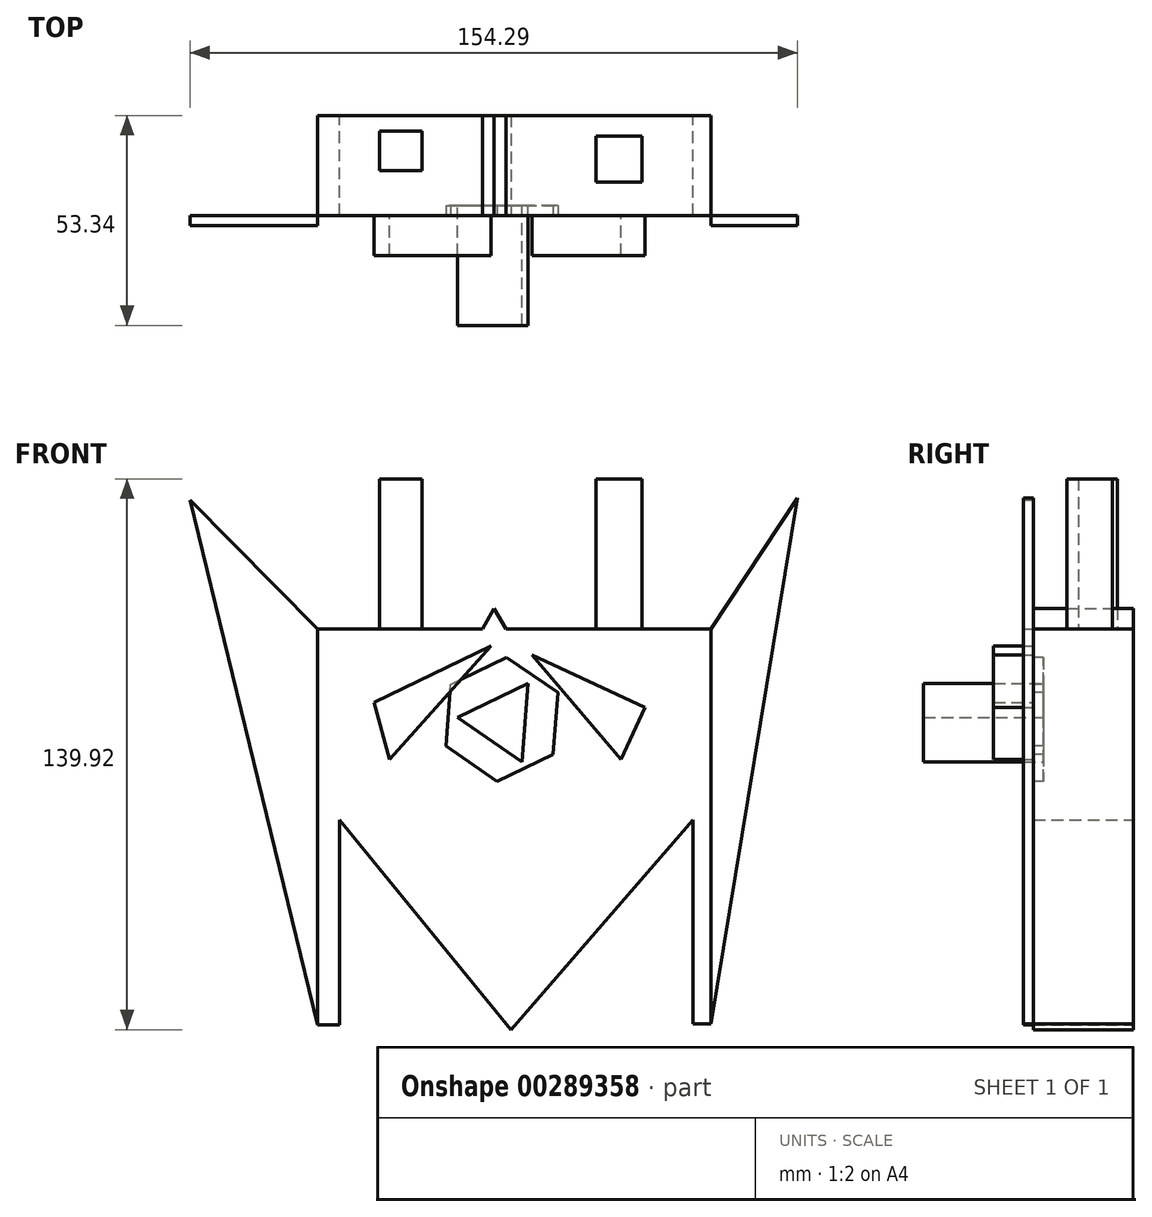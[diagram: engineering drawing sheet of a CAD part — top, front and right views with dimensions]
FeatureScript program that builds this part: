
annotation { "Feature Type Name" : "Feature", "Feature Type Description" : "" }
export const myFeature = defineFeature(function(context is Context, id is Id, definition is map)
    precondition{}
    {
        {
            var Q0;
            Q0=qCreatedBy(makeId("Front.planeOp"),FACE);
            var sketch = newSketch(context, id + "F0", { "sketchPlane" : qUnion([Q0])});
            skLineSegment(sketch, "E0.bottom", {"start": v(-40.98, 12.79) * mm, "end": v(-35.41, 12.79) * mm});
            skLineSegment(sketch, "E0.top", {"start": v(-40.98, -39.35) * mm, "end": v(-35.41, -39.35) * mm});
            skLineSegment(sketch, "E0.left", {"start": v(-40.98, 12.79) * mm, "end": v(-40.98, -39.35) * mm});
            skLineSegment(sketch, "E0.right", {"start": v(-35.41, 12.79) * mm, "end": v(-35.41, -39.35) * mm});
            skLineSegment(sketch, "E1.bottom", {"start": v(-40.98, 12.79) * mm, "end": v(59.02, 12.79) * mm});
            skLineSegment(sketch, "E1.top", {"start": v(-40.98, 61.31) * mm, "end": v(59.02, 61.31) * mm});
            skLineSegment(sketch, "E1.left", {"start": v(-40.98, 12.79) * mm, "end": v(-40.98, 61.31) * mm});
            skLineSegment(sketch, "E1.right", {"start": v(59.02, 12.79) * mm, "end": v(59.02, 61.31) * mm});
            skLineSegment(sketch, "E2.bottom", {"start": v(59.02, 12.79) * mm, "end": v(54.43, 12.79) * mm});
            skLineSegment(sketch, "E2.top", {"start": v(59.02, -39.02) * mm, "end": v(54.43, -39.02) * mm});
            skLineSegment(sketch, "E2.left", {"start": v(59.02, 12.79) * mm, "end": v(59.02, -39.02) * mm});
            skLineSegment(sketch, "E2.right", {"start": v(54.43, 12.79) * mm, "end": v(54.43, -39.02) * mm});
            skArc(sketch, "E3", {"start": v(9.18, -21.31) * mm, "mid": v(3.35, -2.92) * mm, "end": v(-7.87, 12.79) * mm});
            skArc(sketch, "E4", {"start": v(9.18, -21.31) * mm, "mid": v(19.12, -5.56) * mm, "end": v(22.3, 12.79) * mm});
            skArc(sketch, "E5", {"start": v(-2.03, 5.92) * mm, "mid": v(-8, -5.66) * mm, "end": v(-7.87, -18.69) * mm});
            skArc(sketch, "E6", {"start": v(-7.87, 12.79) * mm, "mid": v(-18.77, -1.85) * mm, "end": v(-8.2, -16.72) * mm});
            skCircle(sketch, "E7.cCircle", {"center": v(3.93, 42.3) * mm, "radius": 12.13 * mm, "construction": true});
            skLineSegment(sketch, "E7.0", {"start": v(24.95, 30.16) * mm, "end": v(-17.08, 30.16) * mm});
            skLineSegment(sketch, "E7.1", {"start": v(-17.08, 30.16) * mm, "end": v(3.93, 66.56) * mm});
            skLineSegment(sketch, "E7.2", {"start": v(3.93, 66.56) * mm, "end": v(24.95, 30.16) * mm});
            skPoint(sketch, "E7.0.midPoint", {"position": v(3.93, 30.16) * mm});
            skSolve(sketch);
        }
        {
            var Q0;
            Q0 = qSketchRegion(id + "F0", true);
            extrude(context, id + "F1", {"entities" : qUnion([Q0]), "depth" : 25.4 * mm});
        }
        {
            var Q0;
            Q0=makeQuery(id+"F1.opExtrude","CAP_FACE",FACE,{"disambiguationData":[OSD([sQuery(id+"F0.wireOp",EDGE,"E0.top"),sQuery(id+"F0.wireOp",EDGE,"E0.left"),sQuery(id+"F0.wireOp",EDGE,"E0.right"),sQuery(id+"F0.wireOp",EDGE,"E1.bottom"),sQuery(id+"F0.wireOp",EDGE,"E1.top"),sQuery(id+"F0.wireOp",EDGE,"E1.left"),sQuery(id+"F0.wireOp",EDGE,"E1.right"),sQuery(id+"F0.wireOp",EDGE,"E2.top"),sQuery(id+"F0.wireOp",EDGE,"E2.left"),sQuery(id+"F0.wireOp",EDGE,"E2.right"),sQuery(id+"F0.wireOp",EDGE,"E3"),sQuery(id+"F0.wireOp",EDGE,"E4"),sQuery(id+"F0.wireOp",EDGE,"E5"),sQuery(id+"F0.wireOp",EDGE,"E6"),sQuery(id+"F0.wireOp",EDGE,"E7.1"),sQuery(id+"F0.wireOp",EDGE,"E7.2")])],"isStart":false});
            var sketch = newSketch(context, id + "F2", { "sketchPlane" : qUnion([Q0])});
            skCircle(sketch, "E8.cCircle", {"center": v(5.89, 38.32) * mm, "radius": 13.66 * mm, "construction": true});
            skLineSegment(sketch, "E8.0", {"start": v(-7.12, 47.24) * mm, "end": v(7.12, 54.04) * mm});
            skLineSegment(sketch, "E8.1", {"start": v(7.12, 54.04) * mm, "end": v(20.12, 45.12) * mm});
            skLineSegment(sketch, "E8.2", {"start": v(20.12, 45.12) * mm, "end": v(18.9, 29.4) * mm});
            skLineSegment(sketch, "E8.3", {"start": v(18.9, 29.4) * mm, "end": v(4.66, 22.6) * mm});
            skLineSegment(sketch, "E8.4", {"start": v(4.66, 22.6) * mm, "end": v(-8.34, 31.51) * mm});
            skLineSegment(sketch, "E8.5", {"start": v(-8.34, 31.51) * mm, "end": v(-7.12, 47.24) * mm});
            skPoint(sketch, "E8.0.midPoint", {"position": v(0, 50.64) * mm});
            skSolve(sketch);
        }
        {
            var Q0;
            Q0 = qSketchRegion(id + "F2", true);
            extrude(context, id + "F3", {"entities" : qUnion([Q0]), "operationType" : NewBodyOperationType.REMOVE, "oppositeDirection" : true, "depth" : 2.54 * mm});
        }
        {
            var Q0;
            Q0=makeQuery(id+"F1.opExtrude","CAP_FACE",FACE,{"disambiguationData":[OSD([sQuery(id+"F0.wireOp",EDGE,"E0.top"),sQuery(id+"F0.wireOp",EDGE,"E0.left"),sQuery(id+"F0.wireOp",EDGE,"E0.right"),sQuery(id+"F0.wireOp",EDGE,"E1.bottom"),sQuery(id+"F0.wireOp",EDGE,"E1.top"),sQuery(id+"F0.wireOp",EDGE,"E1.left"),sQuery(id+"F0.wireOp",EDGE,"E1.right"),sQuery(id+"F0.wireOp",EDGE,"E2.top"),sQuery(id+"F0.wireOp",EDGE,"E2.left"),sQuery(id+"F0.wireOp",EDGE,"E2.right"),sQuery(id+"F0.wireOp",EDGE,"E3"),sQuery(id+"F0.wireOp",EDGE,"E4"),sQuery(id+"F0.wireOp",EDGE,"E5"),sQuery(id+"F0.wireOp",EDGE,"E6"),sQuery(id+"F0.wireOp",EDGE,"E7.1"),sQuery(id+"F0.wireOp",EDGE,"E7.2")])],"isStart":false});
            var sketch = newSketch(context, id + "F4", { "sketchPlane" : qUnion([Q0])});
            skLineSegment(sketch, "E9", {"start": v(-40.98, -39.35) * mm, "end": v(-73.33, 94.12) * mm});
            skLineSegment(sketch, "E10", {"start": v(-73.33, 94.12) * mm, "end": v(-40.98, 61.31) * mm});
            skLineSegment(sketch, "E11", {"start": v(59.02, 61.31) * mm, "end": v(80.96, 94.54) * mm});
            skLineSegment(sketch, "E12", {"start": v(80.96, 94.54) * mm, "end": v(59.02, -39.02) * mm});
            skSolve(sketch);
        }
        {
            var Q0;
            Q0=makeQuery(id+"F4.imprint","IMPRINT",FACE,{"disambiguationData":[TD([[makeQuery(id+"F4.imprint","IMPRINT",EDGE,{"derivedFrom":sQuery(id+"F4.wireOp",EDGE,"E9")}),-1.0]])]});
            var Q1;
            Q1=makeQuery(id+"F4.imprint","IMPRINT",FACE,{"disambiguationData":[TD([[makeQuery(id+"F4.imprint","IMPRINT",EDGE,{"derivedFrom":sQuery(id+"F4.wireOp",EDGE,"E11")}),-1.0]])]});
            extrude(context, id + "F5", {"entities" : qUnion([Q0, Q1]), "depth" : 2.54 * mm});
        }
        {
            var Q0;
            Q0=makeQuery(id+"F3.boolean.opBoolean","COPY",FACE,{"derivedFrom":makeQuery(id+"F3.opExtrude","CAP_FACE",FACE,{"disambiguationData":[OSD([sQuery(id+"F2.wireOp",EDGE,"E8.0"),sQuery(id+"F2.wireOp",EDGE,"E8.1"),sQuery(id+"F2.wireOp",EDGE,"E8.2"),sQuery(id+"F2.wireOp",EDGE,"E8.3"),sQuery(id+"F2.wireOp",EDGE,"E8.4"),sQuery(id+"F2.wireOp",EDGE,"E8.5")])],"isStart":false})});
            var sketch = newSketch(context, id + "F6", { "sketchPlane" : qUnion([Q0])});
            skCircle(sketch, "E13.cCircle", {"center": v(6.05, 37.94) * mm, "radius": 5.75 * mm, "construction": true});
            skPoint(sketch, "E13.cCircle.perimeterSnap0", {"position": v(11.78, 26) * mm});
            skLineSegment(sketch, "E13.0", {"start": v(12.55, 47.42) * mm, "end": v(11, 27.57) * mm});
            skLineSegment(sketch, "E13.1", {"start": v(11, 27.57) * mm, "end": v(-5.4, 38.84) * mm});
            skLineSegment(sketch, "E13.2", {"start": v(-5.4, 38.84) * mm, "end": v(12.55, 47.42) * mm});
            skPoint(sketch, "E13.0.midPoint", {"position": v(11.78, 37.5) * mm});
            skPoint(sketch, "E13.0.midPoint.positionSnap0", {"position": v(11.78, 26) * mm});
            skSolve(sketch);
        }
        {
            var Q0;
            Q0 = qSketchRegion(id + "F6", true);
            extrude(context, id + "F7", {"entities" : qUnion([Q0]), "operationType" : NewBodyOperationType.ADD, "depth" : 30.48 * mm});
        }
        {
            var Q0;
            {var subQ0=sQuery(id+"F0.wireOp",EDGE,"E1.top");Q0=makeQuery(id+"F1.opExtrude","SWEPT_FACE",FACE,{"disambiguationData":[OSD([subQ0]),TDD([makeQuery(id+"F0.imprint","IMPRINT",EDGE,{"disambiguationData":[TD([[makeQuery(id+"F0.imprint","INTERSECT",VERTEX,{"derivedFrom":[subQ0,sQuery(id+"F0.wireOp",EDGE,"E1.right")]}),1.0]])],"derivedFrom":subQ0})])]});}
            var sketch = newSketch(context, id + "F8", { "sketchPlane" : qUnion([Q0])});
            skLineSegment(sketch, "E14.bottom", {"start": v(41.46, -16.93) * mm, "end": v(29.82, -16.93) * mm});
            skLineSegment(sketch, "E14.top", {"start": v(41.46, -5.3) * mm, "end": v(29.82, -5.3) * mm});
            skLineSegment(sketch, "E14.left", {"start": v(41.46, -16.93) * mm, "end": v(41.46, -5.3) * mm});
            skLineSegment(sketch, "E14.right", {"start": v(29.82, -16.93) * mm, "end": v(29.82, -5.3) * mm});
            skLineSegment(sketch, "E15.bottom", {"start": v(-14.42, -13.97) * mm, "end": v(-25.22, -13.97) * mm});
            skLineSegment(sketch, "E15.top", {"start": v(-14.42, -4.02) * mm, "end": v(-25.22, -4.02) * mm});
            skLineSegment(sketch, "E15.left", {"start": v(-14.42, -13.97) * mm, "end": v(-14.42, -4.02) * mm});
            skLineSegment(sketch, "E15.right", {"start": v(-25.22, -13.97) * mm, "end": v(-25.22, -4.02) * mm});
            skSolve(sketch);
        }
        {
            var Q0;
            Q0 = qSketchRegion(id + "F8", true);
            extrude(context, id + "F9", {"entities" : qUnion([Q0]), "operationType" : NewBodyOperationType.ADD, "depth" : 38.1 * mm});
        }
        {
            var Q0;
            Q0=makeQuery(id+"F1.opExtrude","CAP_FACE",FACE,{"disambiguationData":[OSD([sQuery(id+"F0.wireOp",EDGE,"E0.top"),sQuery(id+"F0.wireOp",EDGE,"E0.left"),sQuery(id+"F0.wireOp",EDGE,"E0.right"),sQuery(id+"F0.wireOp",EDGE,"E1.bottom"),sQuery(id+"F0.wireOp",EDGE,"E1.top"),sQuery(id+"F0.wireOp",EDGE,"E1.left"),sQuery(id+"F0.wireOp",EDGE,"E1.right"),sQuery(id+"F0.wireOp",EDGE,"E2.top"),sQuery(id+"F0.wireOp",EDGE,"E2.left"),sQuery(id+"F0.wireOp",EDGE,"E2.right"),sQuery(id+"F0.wireOp",EDGE,"E3"),sQuery(id+"F0.wireOp",EDGE,"E4"),sQuery(id+"F0.wireOp",EDGE,"E5"),sQuery(id+"F0.wireOp",EDGE,"E6"),sQuery(id+"F0.wireOp",EDGE,"E7.1"),sQuery(id+"F0.wireOp",EDGE,"E7.2")])],"isStart":false});
            var sketch = newSketch(context, id + "F10", { "sketchPlane" : qUnion([Q0])});
            skLineSegment(sketch, "E16", {"start": v(-22.6, 28.16) * mm, "end": v(3.1, 57.02) * mm});
            skLineSegment(sketch, "E17", {"start": v(3.1, 57.02) * mm, "end": v(-26.61, 42.59) * mm});
            skPoint(sketch, "E17.endSnap0", {"position": v(-9.75, 42.59) * mm});
            skLineSegment(sketch, "E18", {"start": v(-26.61, 42.59) * mm, "end": v(-22.6, 28.16) * mm});
            skLineSegment(sketch, "E19", {"start": v(13.56, 54.64) * mm, "end": v(42.21, 41.37) * mm});
            skLineSegment(sketch, "E20", {"start": v(42.21, 41.37) * mm, "end": v(36.09, 28.16) * mm});
            skLineSegment(sketch, "E21", {"start": v(36.09, 28.16) * mm, "end": v(13.56, 54.64) * mm});
            skSolve(sketch);
        }
        {
            var Q0;
            Q0 = qSketchRegion(id + "F10", true);
            extrude(context, id + "F11", {"entities" : qUnion([Q0]), "operationType" : NewBodyOperationType.ADD, "depth" : 10.16 * mm});
        }
        {
            var Q0;
            Q0=makeQuery(id+"F1.opExtrude","CAP_FACE",FACE,{"disambiguationData":[OSD([sQuery(id+"F0.wireOp",EDGE,"E0.top"),sQuery(id+"F0.wireOp",EDGE,"E0.left"),sQuery(id+"F0.wireOp",EDGE,"E0.right"),sQuery(id+"F0.wireOp",EDGE,"E1.bottom"),sQuery(id+"F0.wireOp",EDGE,"E1.top"),sQuery(id+"F0.wireOp",EDGE,"E1.left"),sQuery(id+"F0.wireOp",EDGE,"E1.right"),sQuery(id+"F0.wireOp",EDGE,"E2.top"),sQuery(id+"F0.wireOp",EDGE,"E2.left"),sQuery(id+"F0.wireOp",EDGE,"E2.right"),sQuery(id+"F0.wireOp",EDGE,"E3"),sQuery(id+"F0.wireOp",EDGE,"E4"),sQuery(id+"F0.wireOp",EDGE,"E5"),sQuery(id+"F0.wireOp",EDGE,"E6"),sQuery(id+"F0.wireOp",EDGE,"E7.1"),sQuery(id+"F0.wireOp",EDGE,"E7.2")])],"isStart":false});
            var sketch = newSketch(context, id + "F12", { "sketchPlane" : qUnion([Q0])});
            skCircle(sketch, "E22.cCircle", {"center": v(42.6, 54.89) * mm, "radius": 2.43 * mm, "construction": true});
            skLineSegment(sketch, "E22.0", {"start": v(42.74, 52.46) * mm, "end": v(42.44, 52.46) * mm});
            skLineSegment(sketch, "E22.1", {"start": v(42.44, 52.46) * mm, "end": v(42.13, 52.5) * mm});
            skLineSegment(sketch, "E22.2", {"start": v(42.13, 52.5) * mm, "end": v(41.84, 52.57) * mm});
            skLineSegment(sketch, "E22.3", {"start": v(41.84, 52.57) * mm, "end": v(41.55, 52.68) * mm});
            skLineSegment(sketch, "E22.4", {"start": v(41.55, 52.68) * mm, "end": v(41.29, 52.83) * mm});
            skLineSegment(sketch, "E22.5", {"start": v(41.29, 52.83) * mm, "end": v(41.04, 53.01) * mm});
            skLineSegment(sketch, "E22.6", {"start": v(41.04, 53.01) * mm, "end": v(40.82, 53.22) * mm});
            skLineSegment(sketch, "E22.7", {"start": v(40.82, 53.22) * mm, "end": v(40.62, 53.46) * mm});
            skLineSegment(sketch, "E22.8", {"start": v(40.62, 53.46) * mm, "end": v(40.46, 53.71) * mm});
            skLineSegment(sketch, "E22.9", {"start": v(40.46, 53.71) * mm, "end": v(40.33, 54) * mm});
            skLineSegment(sketch, "E22.10", {"start": v(40.33, 54) * mm, "end": v(40.23, 54.28) * mm});
            skLineSegment(sketch, "E22.11", {"start": v(40.23, 54.28) * mm, "end": v(40.18, 54.58) * mm});
            skLineSegment(sketch, "E22.12", {"start": v(40.18, 54.58) * mm, "end": v(40.16, 54.89) * mm});
            skLineSegment(sketch, "E22.13", {"start": v(40.16, 54.89) * mm, "end": v(40.18, 55.2) * mm});
            skLineSegment(sketch, "E22.14", {"start": v(40.18, 55.2) * mm, "end": v(40.23, 55.5) * mm});
            skLineSegment(sketch, "E22.15", {"start": v(40.23, 55.5) * mm, "end": v(40.33, 55.78) * mm});
            skLineSegment(sketch, "E22.16", {"start": v(40.33, 55.78) * mm, "end": v(40.46, 56.06) * mm});
            skLineSegment(sketch, "E22.17", {"start": v(40.46, 56.06) * mm, "end": v(40.62, 56.32) * mm});
            skLineSegment(sketch, "E22.18", {"start": v(40.62, 56.32) * mm, "end": v(40.82, 56.55) * mm});
            skLineSegment(sketch, "E22.19", {"start": v(40.82, 56.55) * mm, "end": v(41.04, 56.76) * mm});
            skLineSegment(sketch, "E22.20", {"start": v(41.04, 56.76) * mm, "end": v(41.29, 56.94) * mm});
            skLineSegment(sketch, "E22.21", {"start": v(41.29, 56.94) * mm, "end": v(41.55, 57.09) * mm});
            skLineSegment(sketch, "E22.22", {"start": v(41.55, 57.09) * mm, "end": v(41.84, 57.2) * mm});
            skLineSegment(sketch, "E22.23", {"start": v(41.84, 57.2) * mm, "end": v(42.13, 57.28) * mm});
            skLineSegment(sketch, "E22.24", {"start": v(42.13, 57.28) * mm, "end": v(42.44, 57.31) * mm});
            skLineSegment(sketch, "E22.25", {"start": v(42.44, 57.31) * mm, "end": v(42.74, 57.31) * mm});
            skLineSegment(sketch, "E22.26", {"start": v(42.74, 57.31) * mm, "end": v(43.05, 57.28) * mm});
            skLineSegment(sketch, "E22.27", {"start": v(43.05, 57.28) * mm, "end": v(43.34, 57.2) * mm});
            skLineSegment(sketch, "E22.28", {"start": v(43.34, 57.2) * mm, "end": v(43.63, 57.09) * mm});
            skLineSegment(sketch, "E22.29", {"start": v(43.63, 57.09) * mm, "end": v(43.9, 56.94) * mm});
            skLineSegment(sketch, "E22.30", {"start": v(43.9, 56.94) * mm, "end": v(44.14, 56.76) * mm});
            skLineSegment(sketch, "E22.31", {"start": v(44.14, 56.76) * mm, "end": v(44.36, 56.55) * mm});
            skLineSegment(sketch, "E22.32", {"start": v(44.36, 56.55) * mm, "end": v(44.56, 56.32) * mm});
            skLineSegment(sketch, "E22.33", {"start": v(44.56, 56.32) * mm, "end": v(44.72, 56.06) * mm});
            skLineSegment(sketch, "E22.34", {"start": v(44.72, 56.06) * mm, "end": v(44.85, 55.78) * mm});
            skLineSegment(sketch, "E22.35", {"start": v(44.85, 55.78) * mm, "end": v(44.95, 55.5) * mm});
            skLineSegment(sketch, "E22.36", {"start": v(44.95, 55.5) * mm, "end": v(45, 55.2) * mm});
            skLineSegment(sketch, "E22.37", {"start": v(45, 55.2) * mm, "end": v(45.02, 54.89) * mm});
            skLineSegment(sketch, "E22.38", {"start": v(45.02, 54.89) * mm, "end": v(45, 54.58) * mm});
            skLineSegment(sketch, "E22.39", {"start": v(45, 54.58) * mm, "end": v(44.95, 54.28) * mm});
            skLineSegment(sketch, "E22.40", {"start": v(44.95, 54.28) * mm, "end": v(44.85, 54) * mm});
            skLineSegment(sketch, "E22.41", {"start": v(44.85, 54) * mm, "end": v(44.72, 53.71) * mm});
            skLineSegment(sketch, "E22.42", {"start": v(44.72, 53.71) * mm, "end": v(44.56, 53.46) * mm});
            skLineSegment(sketch, "E22.43", {"start": v(44.56, 53.46) * mm, "end": v(44.36, 53.22) * mm});
            skLineSegment(sketch, "E22.44", {"start": v(44.36, 53.22) * mm, "end": v(44.14, 53.01) * mm});
            skLineSegment(sketch, "E22.45", {"start": v(44.14, 53.01) * mm, "end": v(43.9, 52.83) * mm});
            skLineSegment(sketch, "E22.46", {"start": v(43.9, 52.83) * mm, "end": v(43.63, 52.68) * mm});
            skLineSegment(sketch, "E22.47", {"start": v(43.63, 52.68) * mm, "end": v(43.34, 52.57) * mm});
            skLineSegment(sketch, "E22.48", {"start": v(43.34, 52.57) * mm, "end": v(43.05, 52.5) * mm});
            skLineSegment(sketch, "E22.49", {"start": v(43.05, 52.5) * mm, "end": v(42.74, 52.46) * mm});
            skPoint(sketch, "E22.0.midPoint", {"position": v(42.6, 52.46) * mm});
            skCircle(sketch, "E23.cCircle", {"center": v(-29.66, 54.53) * mm, "radius": 1.83 * mm, "construction": true});
            skLineSegment(sketch, "E23.0", {"start": v(-27.9, 54.04) * mm, "end": v(-27.97, 53.83) * mm});
            skLineSegment(sketch, "E23.1", {"start": v(-27.97, 53.83) * mm, "end": v(-28.07, 53.62) * mm});
            skLineSegment(sketch, "E23.2", {"start": v(-28.07, 53.62) * mm, "end": v(-28.2, 53.43) * mm});
            skLineSegment(sketch, "E23.3", {"start": v(-28.2, 53.43) * mm, "end": v(-28.35, 53.25) * mm});
            skLineSegment(sketch, "E23.4", {"start": v(-28.35, 53.25) * mm, "end": v(-28.52, 53.1) * mm});
            skLineSegment(sketch, "E23.5", {"start": v(-28.52, 53.1) * mm, "end": v(-28.7, 52.96) * mm});
            skLineSegment(sketch, "E23.6", {"start": v(-28.7, 52.96) * mm, "end": v(-28.91, 52.86) * mm});
            skLineSegment(sketch, "E23.7", {"start": v(-28.91, 52.86) * mm, "end": v(-29.13, 52.78) * mm});
            skLineSegment(sketch, "E23.8", {"start": v(-29.13, 52.78) * mm, "end": v(-29.35, 52.72) * mm});
            skLineSegment(sketch, "E23.9", {"start": v(-29.35, 52.72) * mm, "end": v(-29.58, 52.7) * mm});
            skLineSegment(sketch, "E23.10", {"start": v(-29.58, 52.7) * mm, "end": v(-29.81, 52.7) * mm});
            skLineSegment(sketch, "E23.11", {"start": v(-29.81, 52.7) * mm, "end": v(-30.04, 52.74) * mm});
            skLineSegment(sketch, "E23.12", {"start": v(-30.04, 52.74) * mm, "end": v(-30.27, 52.8) * mm});
            skLineSegment(sketch, "E23.13", {"start": v(-30.27, 52.8) * mm, "end": v(-30.48, 52.89) * mm});
            skLineSegment(sketch, "E23.14", {"start": v(-30.48, 52.89) * mm, "end": v(-30.68, 53) * mm});
            skLineSegment(sketch, "E23.15", {"start": v(-30.68, 53) * mm, "end": v(-30.86, 53.14) * mm});
            skLineSegment(sketch, "E23.16", {"start": v(-30.86, 53.14) * mm, "end": v(-31.03, 53.3) * mm});
            skLineSegment(sketch, "E23.17", {"start": v(-31.03, 53.3) * mm, "end": v(-31.17, 53.48) * mm});
            skLineSegment(sketch, "E23.18", {"start": v(-31.17, 53.48) * mm, "end": v(-31.3, 53.68) * mm});
            skLineSegment(sketch, "E23.19", {"start": v(-31.3, 53.68) * mm, "end": v(-31.39, 53.89) * mm});
            skLineSegment(sketch, "E23.20", {"start": v(-31.39, 53.89) * mm, "end": v(-31.45, 54.11) * mm});
            skLineSegment(sketch, "E23.21", {"start": v(-31.45, 54.11) * mm, "end": v(-31.5, 54.34) * mm});
            skLineSegment(sketch, "E23.22", {"start": v(-31.5, 54.34) * mm, "end": v(-31.5, 54.57) * mm});
            skLineSegment(sketch, "E23.23", {"start": v(-31.5, 54.57) * mm, "end": v(-31.48, 54.8) * mm});
            skLineSegment(sketch, "E23.24", {"start": v(-31.48, 54.8) * mm, "end": v(-31.44, 55.02) * mm});
            skLineSegment(sketch, "E23.25", {"start": v(-31.44, 55.02) * mm, "end": v(-31.36, 55.24) * mm});
            skLineSegment(sketch, "E23.26", {"start": v(-31.36, 55.24) * mm, "end": v(-31.26, 55.45) * mm});
            skLineSegment(sketch, "E23.27", {"start": v(-31.26, 55.45) * mm, "end": v(-31.13, 55.64) * mm});
            skLineSegment(sketch, "E23.28", {"start": v(-31.13, 55.64) * mm, "end": v(-30.98, 55.82) * mm});
            skLineSegment(sketch, "E23.29", {"start": v(-30.98, 55.82) * mm, "end": v(-30.8, 55.97) * mm});
            skLineSegment(sketch, "E23.30", {"start": v(-30.8, 55.97) * mm, "end": v(-30.62, 56.1) * mm});
            skLineSegment(sketch, "E23.31", {"start": v(-30.62, 56.1) * mm, "end": v(-30.42, 56.21) * mm});
            skLineSegment(sketch, "E23.32", {"start": v(-30.42, 56.21) * mm, "end": v(-30.2, 56.3) * mm});
            skLineSegment(sketch, "E23.33", {"start": v(-30.2, 56.3) * mm, "end": v(-29.97, 56.34) * mm});
            skLineSegment(sketch, "E23.34", {"start": v(-29.97, 56.34) * mm, "end": v(-29.75, 56.37) * mm});
            skLineSegment(sketch, "E23.35", {"start": v(-29.75, 56.37) * mm, "end": v(-29.51, 56.37) * mm});
            skLineSegment(sketch, "E23.36", {"start": v(-29.51, 56.37) * mm, "end": v(-29.29, 56.33) * mm});
            skLineSegment(sketch, "E23.37", {"start": v(-29.29, 56.33) * mm, "end": v(-29.06, 56.27) * mm});
            skLineSegment(sketch, "E23.38", {"start": v(-29.06, 56.27) * mm, "end": v(-28.85, 56.18) * mm});
            skLineSegment(sketch, "E23.39", {"start": v(-28.85, 56.18) * mm, "end": v(-28.65, 56.07) * mm});
            skLineSegment(sketch, "E23.40", {"start": v(-28.65, 56.07) * mm, "end": v(-28.47, 55.93) * mm});
            skLineSegment(sketch, "E23.41", {"start": v(-28.47, 55.93) * mm, "end": v(-28.3, 55.77) * mm});
            skLineSegment(sketch, "E23.42", {"start": v(-28.3, 55.77) * mm, "end": v(-28.16, 55.59) * mm});
            skLineSegment(sketch, "E23.43", {"start": v(-28.16, 55.59) * mm, "end": v(-28.04, 55.39) * mm});
            skLineSegment(sketch, "E23.44", {"start": v(-28.04, 55.39) * mm, "end": v(-27.94, 55.18) * mm});
            skLineSegment(sketch, "E23.45", {"start": v(-27.94, 55.18) * mm, "end": v(-27.88, 54.96) * mm});
            skLineSegment(sketch, "E23.46", {"start": v(-27.88, 54.96) * mm, "end": v(-27.84, 54.73) * mm});
            skLineSegment(sketch, "E23.47", {"start": v(-27.84, 54.73) * mm, "end": v(-27.83, 54.5) * mm});
            skLineSegment(sketch, "E23.48", {"start": v(-27.83, 54.5) * mm, "end": v(-27.85, 54.27) * mm});
            skLineSegment(sketch, "E23.49", {"start": v(-27.85, 54.27) * mm, "end": v(-27.9, 54.04) * mm});
            skPoint(sketch, "E23.0.midPoint", {"position": v(-27.93, 53.93) * mm});
            skSolve(sketch);
        }
        {
            var Q0;
            Q0 = qSketchRegion(id + "F12", true);
            extrude(context, id + "F13", {"entities" : qUnion([Q0]), "operationType" : NewBodyOperationType.REMOVE, "depth" : 5.08 * mm});
        }
        {
            var Q0;
            Q0=makeQuery(id+"F1.opExtrude","CAP_FACE",FACE,{"disambiguationData":[OSD([sQuery(id+"F0.wireOp",EDGE,"E0.top"),sQuery(id+"F0.wireOp",EDGE,"E0.left"),sQuery(id+"F0.wireOp",EDGE,"E0.right"),sQuery(id+"F0.wireOp",EDGE,"E1.bottom"),sQuery(id+"F0.wireOp",EDGE,"E1.top"),sQuery(id+"F0.wireOp",EDGE,"E1.left"),sQuery(id+"F0.wireOp",EDGE,"E1.right"),sQuery(id+"F0.wireOp",EDGE,"E2.top"),sQuery(id+"F0.wireOp",EDGE,"E2.left"),sQuery(id+"F0.wireOp",EDGE,"E2.right"),sQuery(id+"F0.wireOp",EDGE,"E3"),sQuery(id+"F0.wireOp",EDGE,"E4"),sQuery(id+"F0.wireOp",EDGE,"E5"),sQuery(id+"F0.wireOp",EDGE,"E6"),sQuery(id+"F0.wireOp",EDGE,"E7.1"),sQuery(id+"F0.wireOp",EDGE,"E7.2")])],"isStart":false});
            var sketch = newSketch(context, id + "F14", { "sketchPlane" : qUnion([Q0])});
            skLineSegment(sketch, "E24", {"start": v(-35.41, 12.79) * mm, "end": v(8.2, -40.51) * mm});
            skLineSegment(sketch, "E25", {"start": v(8.2, -40.51) * mm, "end": v(54.43, 12.79) * mm});
            skLineSegment(sketch, "E26", {"start": v(54.43, 12.79) * mm, "end": v(-35.41, 12.79) * mm});
            skSolve(sketch);
        }
        {
            var Q0;
            Q0 = qSketchRegion(id + "F14", true);
            extrude(context, id + "F15", {"entities" : qUnion([Q0]), "operationType" : NewBodyOperationType.ADD, "oppositeDirection" : true, "depth" : 25.4 * mm});
        }
    });
